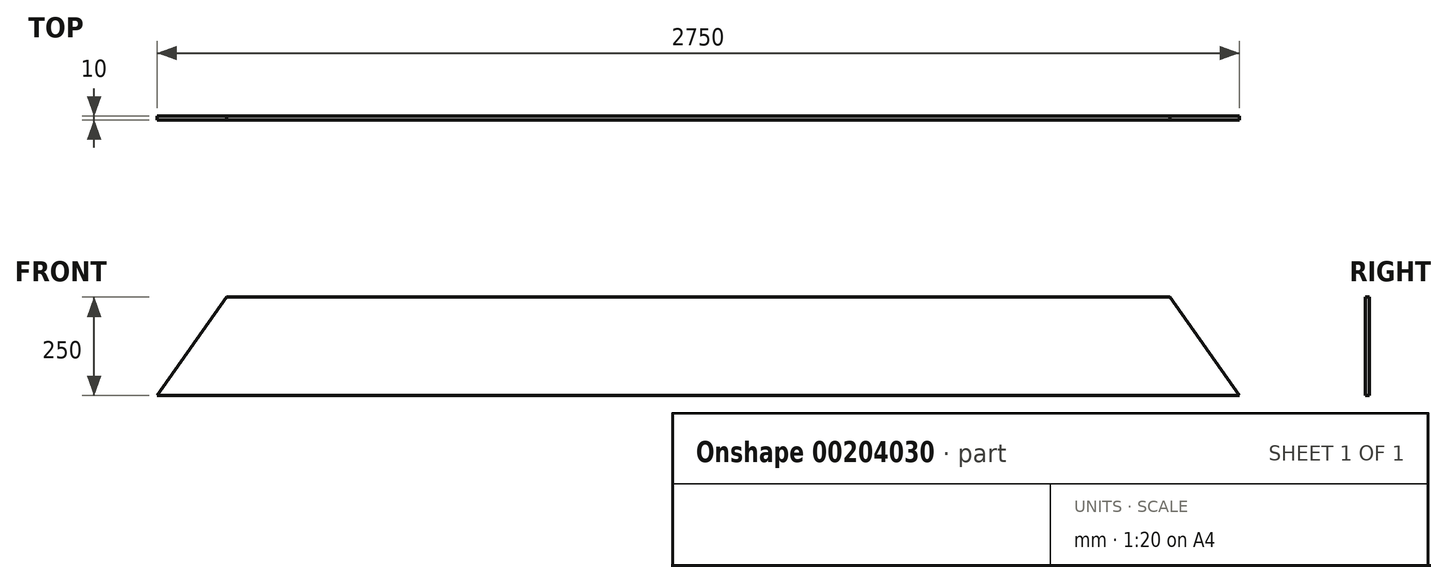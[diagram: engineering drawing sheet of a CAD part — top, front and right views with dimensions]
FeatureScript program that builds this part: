
annotation { "Feature Type Name" : "Feature", "Feature Type Description" : "" }
export const myFeature = defineFeature(function(context is Context, id is Id, definition is map)
    precondition{}
    {
        {
            var Q0;
            Q0=qCreatedBy(makeId("Front.planeOp"),FACE);
            var sketch = newSketch(context, id + "F0", { "sketchPlane" : qUnion([Q0])});
            skLineSegment(sketch, "E0", {"start": v(0, 0) * mm, "end": v(-1375, 0) * mm});
            skLineSegment(sketch, "E1", {"start": v(-1375, 0) * mm, "end": v(-1198.25, 250) * mm});
            skLineSegment(sketch, "E2", {"start": v(-1198.25, 250) * mm, "end": v(0, 250) * mm});
            skLineSegment(sketch, "E3", {"start": v(0, 0) * mm, "end": v(0, 668.09) * mm, "construction": true});
            skLineSegment(sketch, "E4.MirrorCS", {"start": v(1198.25, 250) * mm, "end": v(0, 250) * mm});
            skLineSegment(sketch, "E5.MirrorCS", {"start": v(0, 0) * mm, "end": v(1375, 0) * mm});
            skLineSegment(sketch, "E6.MirrorCS", {"start": v(1375, 0) * mm, "end": v(1198.25, 250) * mm});
            skSolve(sketch);
        }
        {
            var Q0;
            Q0=qSketchRegion(id+"F0",true);
            extrude(context, id + "F1", {"entities" : qUnion([Q0]), "depth" : 10 * mm});
        }
    });
